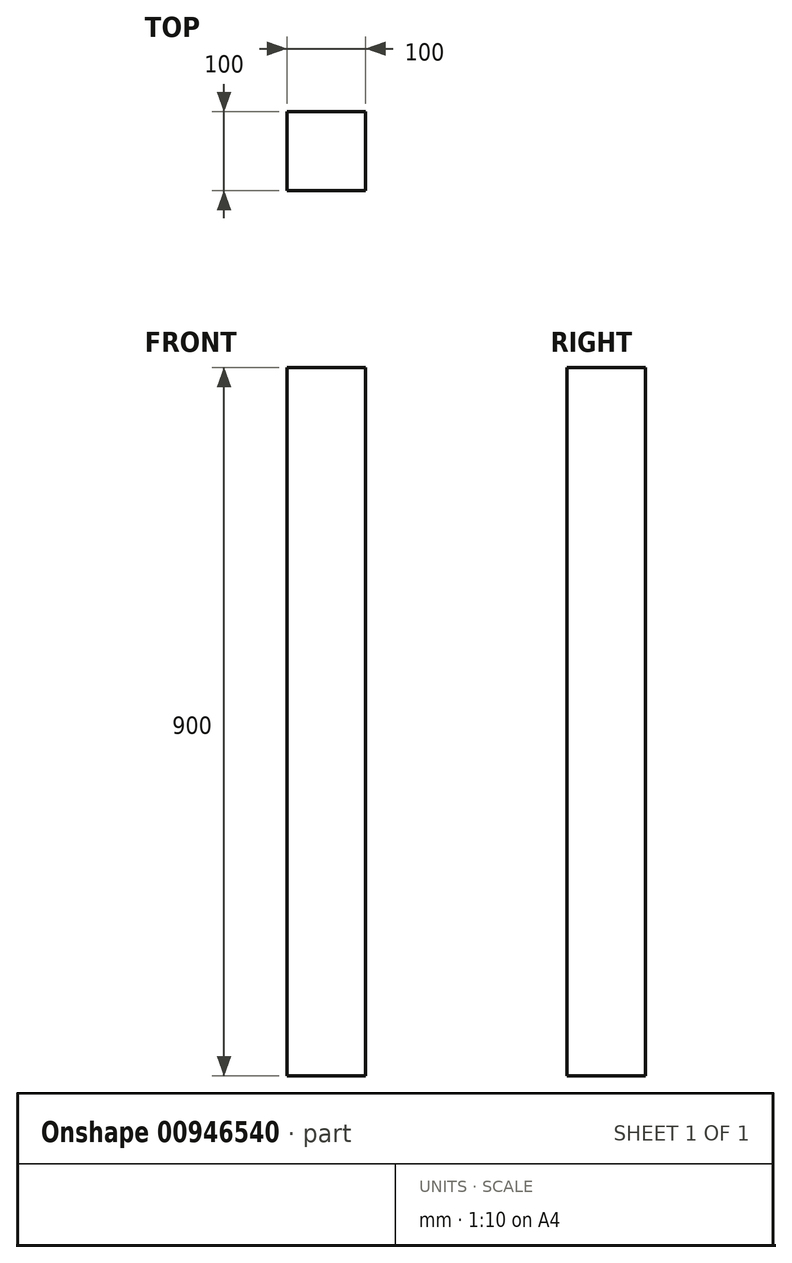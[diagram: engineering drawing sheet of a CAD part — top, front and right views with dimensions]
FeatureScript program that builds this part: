
annotation { "Feature Type Name" : "Feature", "Feature Type Description" : "" }
export const myFeature = defineFeature(function(context is Context, id is Id, definition is map)
    precondition{}
    {
        {
            var Q0;
            Q0=qCreatedBy(makeId("Top.planeOp"),FACE);
            var sketch = newSketch(context, id + "F0", { "sketchPlane" : qUnion([Q0])});
            skLineSegment(sketch, "E0.bottom", {"start": v(50, -50) * mm, "end": v(-50, -50) * mm});
            skLineSegment(sketch, "E0.top", {"start": v(50, 50) * mm, "end": v(-50, 50) * mm});
            skLineSegment(sketch, "E0.left", {"start": v(50, -50) * mm, "end": v(50, 50) * mm});
            skLineSegment(sketch, "E0.right", {"start": v(-50, -50) * mm, "end": v(-50, 50) * mm});
            skPoint(sketch, "E0.middle", {"position": v(0, 0) * mm});
            skSolve(sketch);
        }
        {
            var Q0;
            Q0=qSketchRegion(id+"F0",true);
            extrude(context, id + "F1", {"entities" : qUnion([Q0]), "depth" : 900 * mm, "offsetDistance" : 25 * mm});
        }
    });
